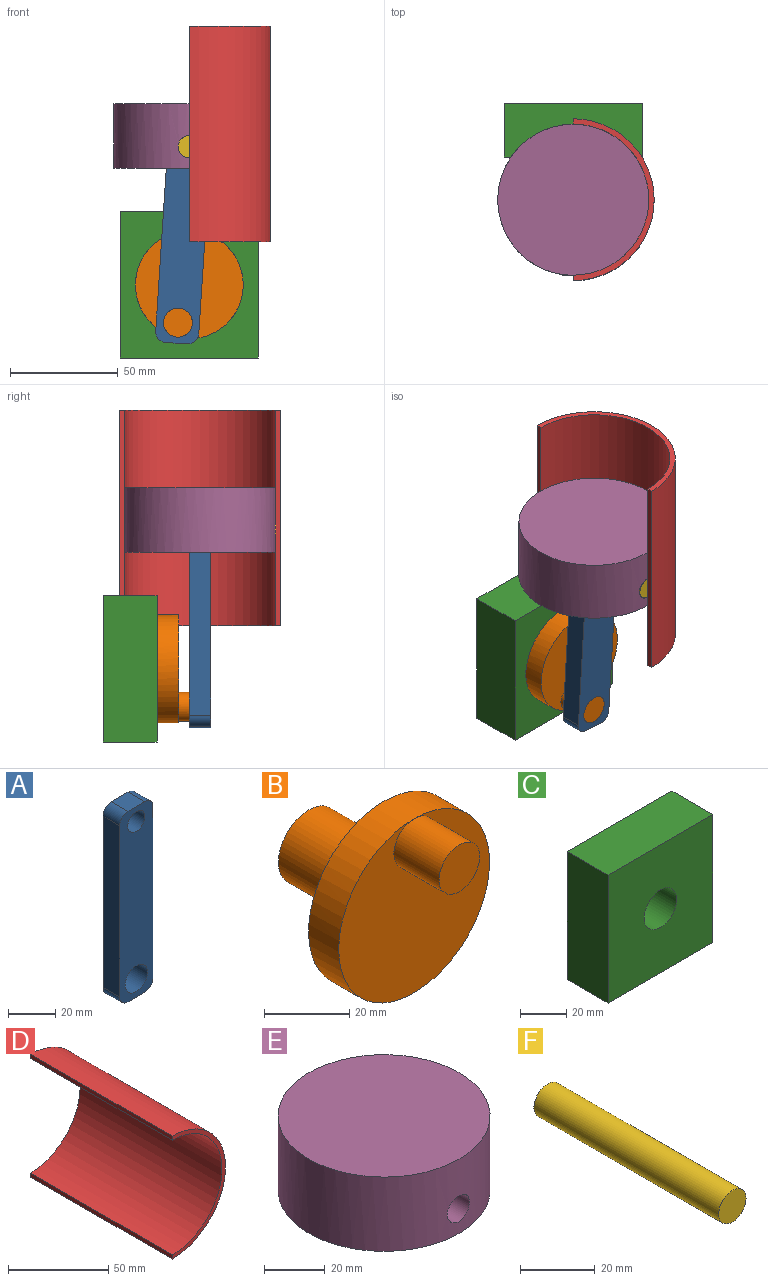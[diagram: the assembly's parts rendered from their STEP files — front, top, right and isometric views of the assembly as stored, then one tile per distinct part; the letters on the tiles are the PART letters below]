
ASSEMBLY  parts=6 mates=5
PART A: 12 faces, bbox 20x10x99 mm
  f0: plane 88.98x10mm, normal (-1,0,0), area 889.8mm2, adj f6,f8,f9,f11
  f1: plane 10x10mm, normal (0,0,-1), area 100mm2, adj f6,f9,f10,f11
  f2: plane 88.98x10mm, normal (1,0,0), area 889.8mm2, adj f6,f7,f10,f11
  f3: plane 10x10mm, normal (0,0,1), area 100mm2, adj f6,f7,f8,f11
  f4: cylinder r=5.18mm len=10.35mm, axis (0,1,0), area 325.2mm2, adj f6,f11
  f5: cylinder r=6.72mm len=13.43mm, axis (0,1,0), area 422.1mm2, adj f6,f11
  f6: plane 98.98x20mm, normal (0,1,0), area 1732.3mm2, adj f0,f1,f2,f3,f4,f5,f7,f8
  f7: cylinder r=5mm len=10mm, axis (0,1,0), area 78.5mm2, adj f2,f3,f6,f11
  f8: cylinder r=5mm len=10mm, axis (0,1,0), area 78.5mm2, adj f0,f3,f6,f11
  f9: cylinder r=5mm len=10mm, axis (0,-1,0), area 78.5mm2, adj f0,f1,f6,f11
  f10: cylinder r=5mm len=10mm, axis (0,-1,0), area 78.5mm2, adj f1,f2,f6,f11
  f11: plane 98.98x20mm, normal (0,-1,0), area 1732.3mm2, adj f0,f1,f2,f3,f4,f5,f7,f8
PART B: 7 faces, bbox 50x50x50 mm
  f0: cylinder r=25mm len=50mm, axis (0,1,0), area 1570.8mm2, adj f1,f2
  f1: plane 50x50mm, normal (0,-1,0), area 1821.7mm2, adj f0,f3
  f2: plane 50x50mm, normal (0,1,0), area 1649.3mm2, adj f0,f5
  f3: cylinder r=6.72mm len=15mm, axis (0,1,0), area 633.1mm2, adj f1,f4
  f4: plane 13.43x13.43mm, normal (0,-1,0), area 141.7mm2, adj f3
  f5: cylinder r=10mm len=25mm, axis (0,-1,0), area 1570.8mm2, adj f2,f6
  f6: plane 20x20mm, normal (0,1,0), area 314.2mm2, adj f5
PART C: 7 faces, bbox 64.1x25x67.8 mm
  f0: plane 67.82x25mm, normal (1,0,0), area 1695.5mm2, adj f1,f3,f5,f6
  f1: plane 64.15x25mm, normal (0,0,1), area 1603.6mm2, adj f0,f2,f5,f6
  f2: plane 67.82x25mm, normal (-1,0,0), area 1695.5mm2, adj f1,f3,f5,f6
  f3: plane 64.15x25mm, normal (0,0,-1), area 1603.6mm2, adj f0,f2,f5,f6
  f4: cylinder r=10mm len=25mm, axis (0,1,0), area 1570.8mm2, adj f5,f6
  f5: plane 67.82x64.15mm, normal (0,-1,0), area 4036.1mm2, adj f0,f1,f2,f3,f4
  f6: plane 67.82x64.15mm, normal (0,1,0), area 4036.1mm2, adj f0,f1,f2,f3,f4
PART D: 6 faces, bbox 37.5x100x75 mm
  f0: cylinder r=37.5mm len=100mm, axis (0,1,0), area 11781mm2, adj f1,f3,f4,f5
  f1: plane 100x2.5mm, normal (-1,0,0), area 250mm2, adj f0,f2,f4,f5
  f2: cylinder r=35mm len=100mm, axis (0,1,0), area 10995.6mm2, adj f1,f3,f4,f5
  f3: plane 100x2.5mm, normal (-1,0,0), area 250mm2, adj f0,f2,f4,f5
  f4: plane 75x37.5mm, normal (0,-1,0), area 284.7mm2, adj f0,f1,f2,f3
  f5: plane 75x37.5mm, normal (0,1,0), area 284.7mm2, adj f0,f1,f2,f3
PART E: 10 faces, bbox 70x70x30 mm
  f0: plane 70x70mm, normal (0,0,-1), area 2081.8mm2, adj f4,f5,f6,f7,f8
  f1: cylinder r=5.18mm len=13.36mm, axis (0,1,0), area 428.1mm2, adj f4,f5
  f2: cylinder r=5.18mm len=13.36mm, axis (0,1,0), area 428.1mm2, adj f4,f7
  f3: plane 70x70mm, normal (0,0,1), area 3848.5mm2, adj f4
  f4: cylinder r=35mm len=70mm, axis (0,0,1), area 6430mm2, adj f0,f1,f2,f3
  f5: plane 40.81x25mm, normal (0,-1,0), area 936.1mm2, adj f0,f1,f6,f8,f9
  f6: plane 43.29x25mm, normal (-1,0,0), area 1082.2mm2, adj f0,f5,f7,f9
  f7: plane 40.81x25mm, normal (0,1,0), area 936.1mm2, adj f0,f2,f6,f8,f9
  f8: plane 43.29x25mm, normal (1,0,0), area 1082.2mm2, adj f0,f5,f7,f9
  f9: plane 43.29x40.81mm, normal (0,0,-1), area 1766.6mm2, adj f5,f6,f7,f8
PART F: 3 faces, bbox 10.4x70x10.4 mm
  f0: cylinder r=5.18mm len=70mm, axis (0,1,0), area 2276.3mm2, adj f1,f2
  f1: plane 10.35x10.35mm, normal (0,-1,0), area 84.2mm2, adj f0
  f2: plane 10.35x10.35mm, normal (0,1,0), area 84.2mm2, adj f0
PLACE A rot(axis=(0,1,0),3.7deg) t=(31.07,77.51,22.42)mm
PLACE B rot(axis=(0,-1,0),163.2deg) t=(-62.02,92.51,98.28)mm
PLACE C t=(38.36,117.51,61.57)mm fixed
PLACE D rot(axis=(1,0,0),90deg) t=(-69.9,132.06,192.51)mm fixed
PLACE E t=(38.36,107.59,25.61)mm
PLACE F t=(38.36,107.51,25.61)mm
MATE revolute A.f5 <-> B.f3  axis (0,-1,0) through (-19.83,67.51,55)mm
MATE slider D.f0 <-> E.f4  axis (0,0,1) through (-14.54,72.59,192.51)mm
MATE revolute E.f1 <-> F.f0  axis (0,1,0) through (-14.54,37.51,136.55)mm
MATE revolute B.f0 <-> C.f4  axis (0,1,0) through (-14.54,117.51,72.5)mm
MATE revolute F.f0 <-> A.f4  axis (0,-1,0) through (-14.54,37.51,136.55)mm
